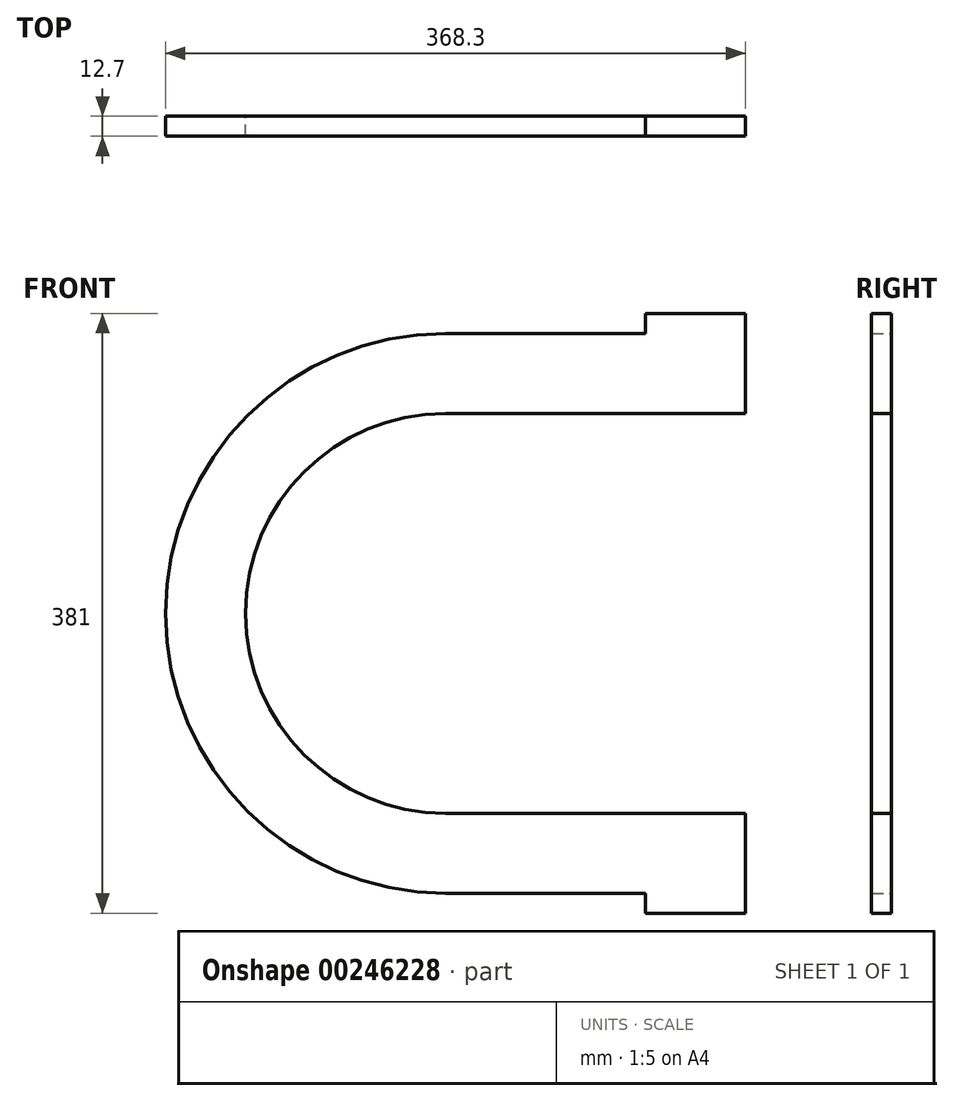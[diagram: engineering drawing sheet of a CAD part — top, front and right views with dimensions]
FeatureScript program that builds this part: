
annotation { "Feature Type Name" : "Feature", "Feature Type Description" : "" }
export const myFeature = defineFeature(function(context is Context, id is Id, definition is map)
    precondition{}
    {
        {
            var Q0;
            Q0=qCreatedBy(makeId("Front.planeOp"),FACE);
            var sketch = newSketch(context, id + "F0", { "sketchPlane" : qUnion([Q0])});
            skLineSegment(sketch, "E0.bottom", {"start": v(0, 177.8) * mm, "end": v(127, 177.8) * mm});
            skLineSegment(sketch, "E0.top", {"start": v(0, -177.8) * mm, "end": v(127, -177.8) * mm});
            skLineSegment(sketch, "E0.right", {"start": v(190.5, 177.8) * mm, "end": v(190.5, 127) * mm});
            skPoint(sketch, "E0.middle", {"position": v(0, 0) * mm});
            skArc(sketch, "E1", {"start": v(0, 127) * mm, "mid": v(-127, 0) * mm, "end": v(0, -127) * mm});
            skLineSegment(sketch, "E2", {"start": v(0, -127) * mm, "end": v(190.5, -127) * mm});
            skLineSegment(sketch, "E3", {"start": v(0, 127) * mm, "end": v(190.5, 127) * mm});
            skLineSegment(sketch, "E4.bottom", {"start": v(190.5, -127) * mm, "end": v(127, -127) * mm});
            skLineSegment(sketch, "E4.top", {"start": v(190.5, -190.5) * mm, "end": v(127, -190.5) * mm});
            skLineSegment(sketch, "E4.left", {"start": v(190.5, -127) * mm, "end": v(190.5, -190.5) * mm});
            skLineSegment(sketch, "E4.right", {"start": v(127, -177.8) * mm, "end": v(127, -190.5) * mm});
            skLineSegment(sketch, "E5.bottom", {"start": v(190.5, 127) * mm, "end": v(127, 127) * mm});
            skLineSegment(sketch, "E5.top", {"start": v(190.5, 190.5) * mm, "end": v(127, 190.5) * mm});
            skLineSegment(sketch, "E5.left", {"start": v(190.5, 127) * mm, "end": v(190.5, 190.5) * mm});
            skLineSegment(sketch, "E5.right", {"start": v(127, 177.8) * mm, "end": v(127, 190.5) * mm});
            skArc(sketch, "E6", {"start": v(0, 177.8) * mm, "mid": v(-177.8, 0) * mm, "end": v(0, -177.8) * mm});
            skPoint(sketch, "E0.left.start.orphan", {"position": v(-190.5, 177.8) * mm});
            skPoint(sketch, "E7.orphan", {"position": v(-190.5, -177.8) * mm});
            skLineSegment(sketch, "E8.trimOffspring", {"start": v(190.5, -127) * mm, "end": v(190.5, -177.8) * mm});
            skSolve(sketch);
        }
        {
            var Q0;
            Q0=makeQuery(id+"F0.imprint","IMPRINT",FACE,{"disambiguationData":[TD([[makeQuery(id+"F0.imprint","IMPRINT",EDGE,{"derivedFrom":sQuery(id+"F0.wireOp",EDGE,"E0.bottom")}),-1.0]])]});
            extrude(context, id + "F1", {"entities" : qUnion([Q0]), "depth" : 12.7 * mm});
        }
    });
